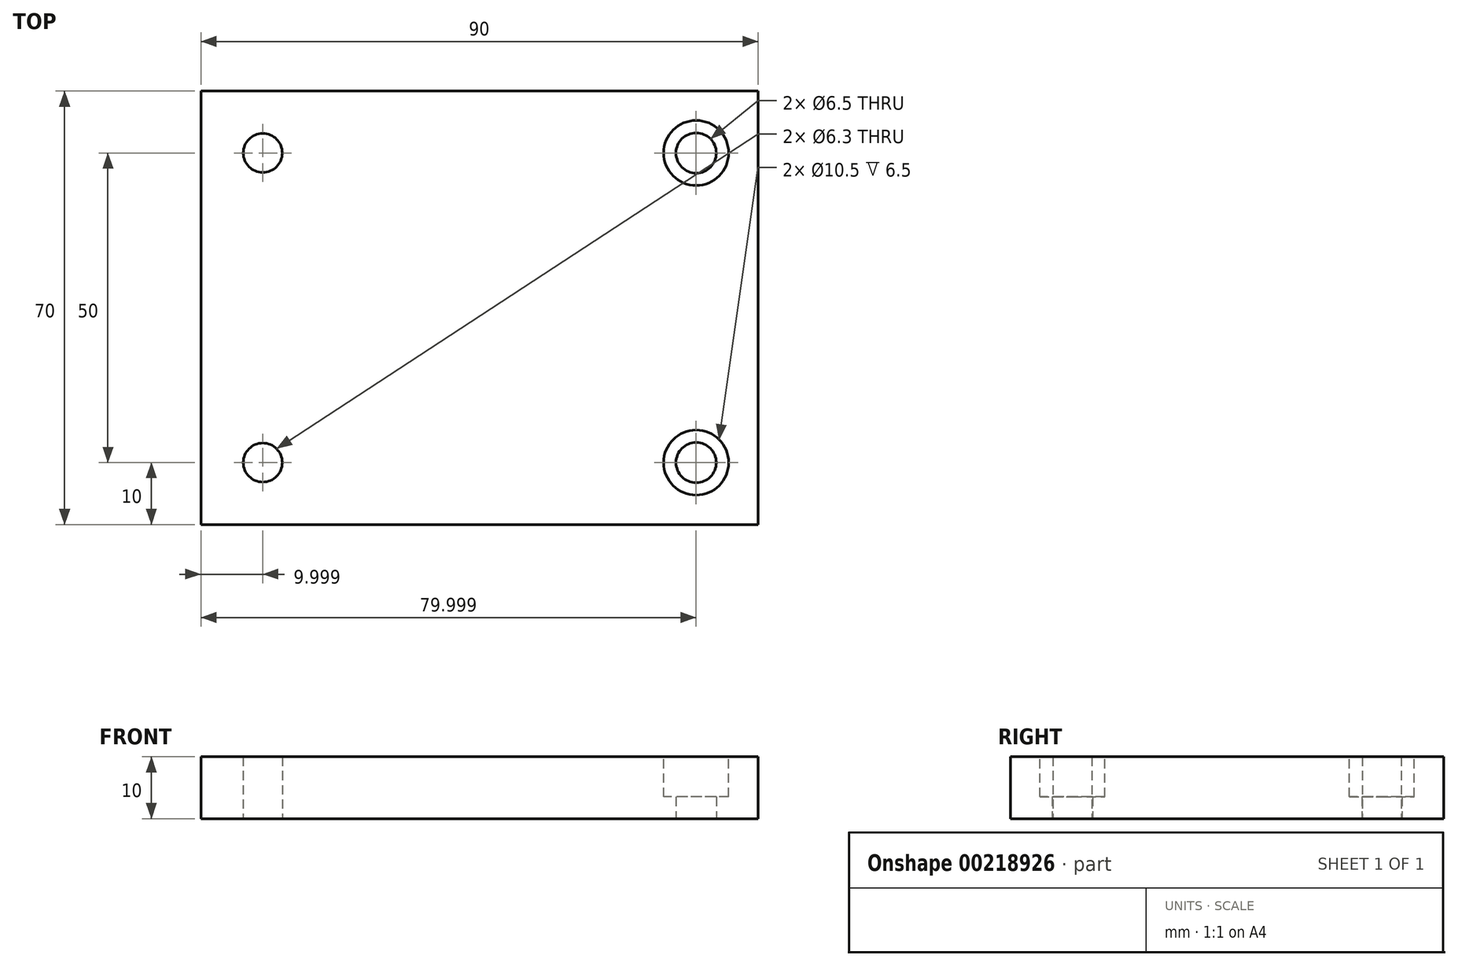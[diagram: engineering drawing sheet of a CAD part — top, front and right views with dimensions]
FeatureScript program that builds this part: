
annotation { "Feature Type Name" : "Feature", "Feature Type Description" : "" }
export const myFeature = defineFeature(function(context is Context, id is Id, definition is map)
    precondition{}
    {
        {
            var Q0;
            Q0=qCreatedBy(makeId("Top.planeOp"),FACE);
            var sketch = newSketch(context, id + "F0", { "sketchPlane" : qUnion([Q0])});
            skLineSegment(sketch, "E0.bottom", {"start": v(-48.78, 21.74) * mm, "end": v(41.22, 21.74) * mm});
            skLineSegment(sketch, "E0.top", {"start": v(-48.78, -48.26) * mm, "end": v(41.22, -48.26) * mm});
            skLineSegment(sketch, "E0.left", {"start": v(-48.78, 21.74) * mm, "end": v(-48.78, -48.26) * mm});
            skLineSegment(sketch, "E0.right", {"start": v(41.22, 21.74) * mm, "end": v(41.22, -48.26) * mm});
            skCircle(sketch, "E1", {"center": v(31.22, 11.74) * mm, "radius": 3.25 * mm});
            skCircle(sketch, "E2", {"center": v(31.22, -38.26) * mm, "radius": 3.25 * mm});
            skCircle(sketch, "E3", {"center": v(-38.78, 11.74) * mm, "radius": 3.15 * mm});
            skCircle(sketch, "E4", {"center": v(-38.78, -38.26) * mm, "radius": 3.15 * mm});
            skSolve(sketch);
        }
        {
            var Q0;
            Q0=makeQuery(id+"F0.imprint","IMPRINT",FACE,{"disambiguationData":[TD([[makeQuery(id+"F0.imprint","IMPRINT",EDGE,{"derivedFrom":sQuery(id+"F0.wireOp",EDGE,"E0.bottom")}),-1.0]])]});
            extrude(context, id + "F1", {"entities" : qUnion([Q0]), "depth" : 10 * mm});
        }
        {
            var Q0;
            Q0=makeQuery(id+"F1.opExtrude","CAP_FACE",FACE,{"disambiguationData":[OSD([sQuery(id+"F0.wireOp",EDGE,"E0.bottom"),sQuery(id+"F0.wireOp",EDGE,"E0.top"),sQuery(id+"F0.wireOp",EDGE,"E0.left"),sQuery(id+"F0.wireOp",EDGE,"E0.right"),sQuery(id+"F0.wireOp",EDGE,"E1"),sQuery(id+"F0.wireOp",EDGE,"E2"),sQuery(id+"F0.wireOp",EDGE,"E3"),sQuery(id+"F0.wireOp",EDGE,"E4")])],"isStart":false});
            var sketch = newSketch(context, id + "F2", { "sketchPlane" : qUnion([Q0])});
            skCircle(sketch, "E5", {"center": v(31.22, -38.26) * mm, "radius": 5.25 * mm});
            skCircle(sketch, "E6", {"center": v(31.22, 11.74) * mm, "radius": 5.25 * mm});
            skSolve(sketch);
        }
        {
            var Q0;
            Q0 = qSketchRegion(id + "F2", true);
            extrude(context, id + "F3", {"entities" : qUnion([Q0]), "operationType" : NewBodyOperationType.REMOVE, "oppositeDirection" : true, "depth" : 6.5 * mm});
        }
    });
